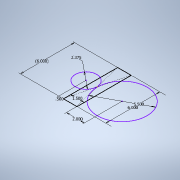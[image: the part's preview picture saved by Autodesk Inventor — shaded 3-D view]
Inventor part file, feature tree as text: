
AUTODESK INVENTOR PART (.ipt)
format: ipt  version: 2020.1 (Build 241239000, 239)  size: 93,696 bytes
history: native  units: in
note: dims shown in document units (in); Inventor stores cm internally (conversion verified against a paired STEP export)
features: sketch x1
ambient origin geometry x8: Origin, YZ Plane, XZ Plane, XY Plane, X Axis, Y Axis, Z Axis, Center Point
feature tree (1):
  sketch  "Sketch1"  dims[d0=1.5in d1=6.0in d2=5.5in d3=2.0in d4=2.375in d5=0.5in d6=6.0in]
